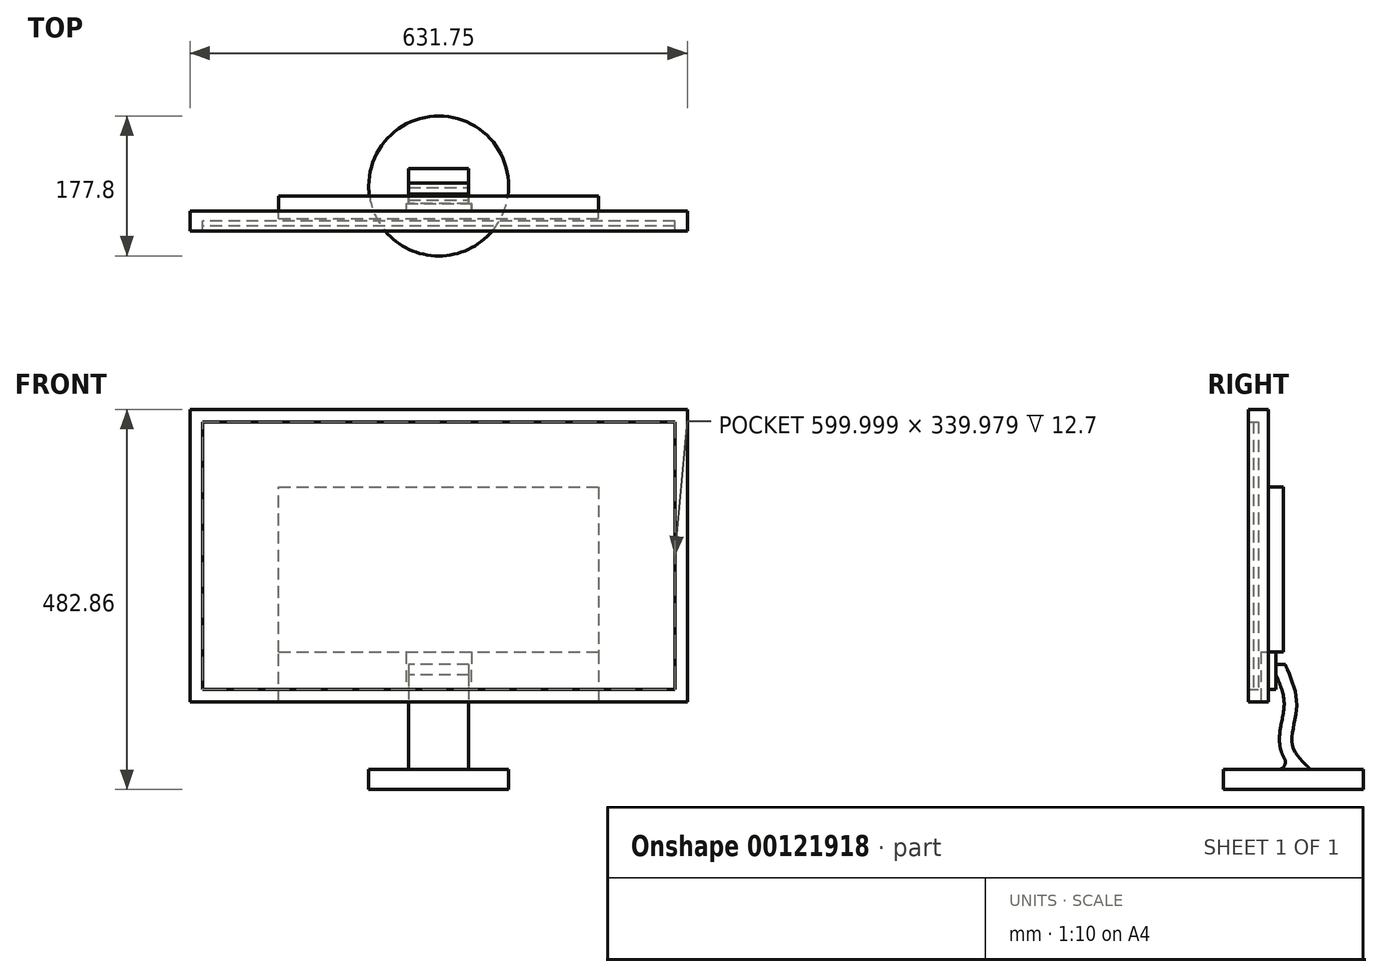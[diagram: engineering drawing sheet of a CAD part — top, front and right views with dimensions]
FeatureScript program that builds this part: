
annotation { "Feature Type Name" : "Feature", "Feature Type Description" : "" }
export const myFeature = defineFeature(function(context is Context, id is Id, definition is map)
    precondition{}
    {
        {
            var Q0;
            Q0=qCreatedBy(makeId("Front.planeOp"),FACE);
            var sketch = newSketch(context, id + "F0", { "sketchPlane" : qUnion([Q0])});
            skLineSegment(sketch, "E0.bottom", {"start": v(-325.58, 229.48) * mm, "end": v(306.17, 229.48) * mm});
            skLineSegment(sketch, "E0.top", {"start": v(-325.58, -142.25) * mm, "end": v(306.17, -142.25) * mm});
            skLineSegment(sketch, "E0.left", {"start": v(-325.58, 229.48) * mm, "end": v(-325.58, -142.25) * mm});
            skLineSegment(sketch, "E0.right", {"start": v(306.17, 229.48) * mm, "end": v(306.17, -142.25) * mm});
            skLineSegment(sketch, "E1", {"start": v(-309.7, 213.6) * mm, "end": v(-309.7, -126.38) * mm});
            skLineSegment(sketch, "E2", {"start": v(-309.7, -126.38) * mm, "end": v(290.3, -126.38) * mm});
            skLineSegment(sketch, "E3", {"start": v(290.3, -126.38) * mm, "end": v(290.3, 213.6) * mm});
            skLineSegment(sketch, "E4", {"start": v(290.3, 213.6) * mm, "end": v(-309.7, 213.6) * mm});
            skSolve(sketch);
        }
        {
            var Q0;
            Q0=makeQuery(id+"F0.imprint","IMPRINT",FACE,{"disambiguationData":[TD([[makeQuery(id+"F0.imprint","IMPRINT",EDGE,{"derivedFrom":sQuery(id+"F0.wireOp",EDGE,"E0.bottom")}),-1.0]])]});
            extrude(context, id + "F1", {"entities" : qUnion([Q0]), "depth" : 25.4 * mm});
        }
        {
            var Q0;
            Q0=makeQuery(id+"F0.imprint","IMPRINT",FACE,{"disambiguationData":[TD([[makeQuery(id+"F0.imprint","IMPRINT",EDGE,{"derivedFrom":sQuery(id+"F0.wireOp",EDGE,"E1")}),1.0]])]});
            extrude(context, id + "F2", {"entities" : qUnion([Q0]), "operationType" : NewBodyOperationType.ADD, "depth" : 12.7 * mm});
        }
        {
            var Q0;
            Q0=makeQuery(id+"F0.imprint","IMPRINT",FACE,{"disambiguationData":[TD([[makeQuery(id+"F0.imprint","IMPRINT",EDGE,{"derivedFrom":sQuery(id+"F0.wireOp",EDGE,"E1")}),1.0]])]});
            var sketch = newSketch(context, id + "F3", { "sketchPlane" : qUnion([Q0])});
            skLineSegment(sketch, "E5", {"start": v(-212.9, 130.8) * mm, "end": v(193.5, 130.8) * mm});
            skLineSegment(sketch, "E6", {"start": v(193.5, 130.8) * mm, "end": v(193.5, -78.75) * mm});
            skLineSegment(sketch, "E7", {"start": v(193.5, -78.75) * mm, "end": v(-212.9, -78.75) * mm});
            skLineSegment(sketch, "E8", {"start": v(-212.9, -78.75) * mm, "end": v(-212.9, 130.8) * mm});
            skSolve(sketch);
        }
        {
            var Q0;
            Q0=makeQuery(id+"F3.imprint","IMPRINT",FACE,{"disambiguationData":[TD([[makeQuery(id+"F3.imprint","IMPRINT",EDGE,{"derivedFrom":sQuery(id+"F3.wireOp",EDGE,"E5")}),-1.0]])]});
            extrude(context, id + "F4", {"entities" : qUnion([Q0]), "operationType" : NewBodyOperationType.ADD, "oppositeDirection" : true, "depth" : 19.05 * mm});
        }
        {
            var Q0;
            Q0=makeQuery(id+"F0.imprint","IMPRINT",FACE,{"disambiguationData":[TD([[makeQuery(id+"F0.imprint","IMPRINT",EDGE,{"derivedFrom":sQuery(id+"F0.wireOp",EDGE,"E1")}),1.0]])]});
            var sketch = newSketch(context, id + "F5", { "sketchPlane" : qUnion([Q0])});
            skPoint(sketch, "E9.0", {"position": v(193.5, -78.75) * mm});
            skPoint(sketch, "E10.0", {"position": v(-212.9, -78.75) * mm});
            skLineSegment(sketch, "E11", {"start": v(193.5, -78.75) * mm, "end": v(193.5, -142.25) * mm});
            skLineSegment(sketch, "E12", {"start": v(193.5, -142.25) * mm, "end": v(-212.9, -142.25) * mm});
            skLineSegment(sketch, "E13", {"start": v(-212.9, -142.25) * mm, "end": v(-212.9, -78.75) * mm});
            skLineSegment(sketch, "E14", {"start": v(-212.9, -78.75) * mm, "end": v(193.5, -78.75) * mm});
            skSolve(sketch);
        }
        {
            var Q0;
            {var subQ5=sQuery(id+"F5.wireOp",EDGE,"E12");Q0=makeQuery(id+"F5.imprint","IMPRINT",FACE,{"disambiguationData":[TD([[makeQuery(id+"F5.imprint","IMPRINT",EDGE,{"derivedFrom":subQ5}),-1.0]])]});}
            var Q1;
            {var subQ5=sQuery(id+"F5.wireOp",EDGE,"E14");Q1=makeQuery(id+"F5.imprint","IMPRINT",FACE,{"disambiguationData":[TD([[makeQuery(id+"F5.imprint","IMPRINT",EDGE,{"derivedFrom":subQ5}),-1.0]])]});}
            extrude(context, id + "F6", {"entities" : qUnion([Q0, Q1]), "operationType" : NewBodyOperationType.REMOVE, "depth" : 9.52 * mm});
        }
        {
            var Q0;
            {var subQ5=sQuery(id+"F5.wireOp",EDGE,"E14");Q0=makeQuery(id+"F5.imprint","IMPRINT",FACE,{"disambiguationData":[TD([[makeQuery(id+"F5.imprint","IMPRINT",EDGE,{"derivedFrom":subQ5}),-1.0]])]});}
            var sketch = newSketch(context, id + "F7", { "sketchPlane" : qUnion([Q0])});
            skLineSegment(sketch, "E15", {"start": v(31.57, -126.38) * mm, "end": v(-50.98, -126.38) * mm});
            skPoint(sketch, "E16.0", {"position": v(-212.9, -78.75) * mm});
            skLineSegment(sketch, "E17", {"start": v(-50.98, -78.75) * mm, "end": v(31.57, -78.75) * mm});
            skLineSegment(sketch, "E18", {"start": v(-50.98, -78.75) * mm, "end": v(-50.98, -126.38) * mm});
            skLineSegment(sketch, "E19", {"start": v(32, -78.67) * mm, "end": v(31.57, -126.38) * mm});
            skSolve(sketch);
        }
        {
            var Q0;
            {var subQ5=sQuery(id+"F7.wireOp",EDGE,"E15");Q0=makeQuery(id+"F7.imprint","IMPRINT",FACE,{"disambiguationData":[TD([[makeQuery(id+"F7.imprint","IMPRINT",EDGE,{"derivedFrom":subQ5}),1.0]])]});}
            extrude(context, id + "F8", {"entities" : qUnion([Q0]), "operationType" : NewBodyOperationType.ADD, "oppositeDirection" : true, "depth" : 9.52 * mm});
        }
        {
            var Q0;
            Q0=makeQuery(id+"F8.opExtrude","CAP_FACE",FACE,{"disambiguationData":[OSD([sQuery(id+"F5.wireOp",EDGE,"E14"),sQuery(id+"F7.wireOp",EDGE,"E15"),sQuery(id+"F7.wireOp",EDGE,"E17"),sQuery(id+"F7.wireOp",EDGE,"E18"),sQuery(id+"F7.wireOp",EDGE,"E19")])],"isStart":false});
            var sketch = newSketch(context, id + "F9", { "sketchPlane" : qUnion([Q0])});
            skLineSegment(sketch, "E20", {"start": v(-28.68, -94.63) * mm, "end": v(47.8, -94.63) * mm});
            skLineSegment(sketch, "E21", {"start": v(47.8, -94.63) * mm, "end": v(47.8, -126.38) * mm});
            skLineSegment(sketch, "E22", {"start": v(47.8, -126.38) * mm, "end": v(-28.68, -126.38) * mm});
            skLineSegment(sketch, "E23", {"start": v(-28.68, -94.63) * mm, "end": v(-28.68, -126.38) * mm});
            skSolve(sketch);
        }
        {
            var Q0;
            Q0=makeQuery(id+"F9.imprint","IMPRINT",FACE,{"disambiguationData":[TD([[makeQuery(id+"F9.imprint","IMPRINT",EDGE,{"derivedFrom":sQuery(id+"F9.wireOp",EDGE,"E20")}),-1.0]])]});
            extrude(context, id + "F10", {"entities" : qUnion([Q0]), "operationType" : NewBodyOperationType.ADD, "depth" : 44.45 * mm});
        }
        {
            var Q0;
            Q0=makeQuery(id+"F10.boolean.opBoolean","MERGE",FACE,{"derivedFrom":[makeQuery(id+"F8.opExtrude","SWEPT_FACE",FACE,{"disambiguationData":[OSD([sQuery(id+"F7.wireOp",EDGE,"E15")])]}),makeQuery(id+"F10.opExtrude","SWEPT_FACE",FACE,{"disambiguationData":[OSD([sQuery(id+"F9.wireOp",EDGE,"E22")])]})]});
            var sketch = newSketch(context, id + "F11", { "sketchPlane" : qUnion([Q0])});
            skLineSegment(sketch, "E24", {"start": v(28.68, -9.53) * mm, "end": v(-47.8, -9.53) * mm});
            skLineSegment(sketch, "E25", {"start": v(-47.8, -9.52) * mm, "end": v(-47.8, -53.98) * mm});
            skLineSegment(sketch, "E26", {"start": v(-47.8, -53.98) * mm, "end": v(28.68, -53.98) * mm});
            skLineSegment(sketch, "E27", {"start": v(28.68, -53.98) * mm, "end": v(28.68, -9.52) * mm});
            skSolve(sketch);
        }
        {
            var Q0;
            Q0=makeQuery(id+"F11.imprint","IMPRINT",FACE,{"disambiguationData":[TD([[makeQuery(id+"F11.imprint","IMPRINT",EDGE,{"derivedFrom":sQuery(id+"F11.wireOp",EDGE,"E24")}),1.0]])]});
            extrude(context, id + "F12", {"entities" : qUnion([Q0]), "operationType" : NewBodyOperationType.ADD, "depth" : 101.6 * mm});
        }
        {
            var Q0;
            Q0=makeQuery(id+"F12.opExtrude","CAP_FACE",FACE,{"disambiguationData":[OSD([sQuery(id+"F11.wireOp",EDGE,"E24"),sQuery(id+"F11.wireOp",EDGE,"E25"),sQuery(id+"F11.wireOp",EDGE,"E26"),sQuery(id+"F11.wireOp",EDGE,"E27")])],"isStart":false});
            var sketch = newSketch(context, id + "F13", { "sketchPlane" : qUnion([Q0])});
            skCircle(sketch, "E28", {"center": v(-9.56, -31.75) * mm, "radius": 88.9 * mm});
            skPoint(sketch, "E28.centerSnap0", {"position": v(-9.56, -53.98) * mm});
            skPoint(sketch, "E28.centerSnap1", {"position": v(28.68, -31.75) * mm});
            skSolve(sketch);
        }
        {
            var Q0;
            Q0=qSketchRegion(id+"F13",true);
            extrude(context, id + "F14", {"entities" : qUnion([Q0]), "operationType" : NewBodyOperationType.ADD, "depth" : 25.4 * mm});
        }
        {
            var Q0;
            Q0=makeQuery(id+"F12.boolean.opBoolean","MERGE",FACE,{"derivedFrom":[makeQuery(id+"F10.opExtrude","SWEPT_FACE",FACE,{"disambiguationData":[OSD([sQuery(id+"F9.wireOp",EDGE,"E21")])]}),makeQuery(id+"F12.opExtrude","SWEPT_FACE",FACE,{"disambiguationData":[OSD([sQuery(id+"F11.wireOp",EDGE,"E25")])]})]});
            var sketch = newSketch(context, id + "F15", { "sketchPlane" : qUnion([Q0])});
            skFitSpline(sketch, "E29", {"points": [v(-21.2, -94.63) * mm, v(-35.71, -146.34) * mm, v(-30.35, -196.38) * mm, v(-53.98, -227.98) * mm], "startDerivative": vector(-63.14, -143.08) * mm, "endDerivative": vector(-104.86, -93.64) * mm});
            skFitSpline(sketch, "E30.0", {"points": [v(-6.68, -101.04) * mm, v(-8, -104.02) * mm, v(-10.57, -109.85) * mm, v(-14.01, -118.26) * mm, v(-16.36, -124.97) * mm, v(-17.83, -130.15) * mm, v(-18.7, -133.95) * mm, v(-19.35, -137.66) * mm, v(-19.68, -140.68) * mm, v(-19.82, -143.06) * mm, v(-19.86, -144.54) * mm, v(-19.85, -145.72) * mm, v(-19.82, -146.9) * mm, v(-19.74, -148.44) * mm, v(-19.58, -150.36) * mm, v(-19.27, -153.02) * mm, v(-18.75, -156.52) * mm, v(-17.95, -160.96) * mm, v(-17.04, -165.6) * mm, v(-16.1, -170.43) * mm, v(-15.19, -175.44) * mm, v(-14.43, -180.62) * mm, v(-13.93, -186.02) * mm, v(-13.84, -190.72) * mm, v(-14.07, -194.6) * mm, v(-14.36, -197.09) * mm, v(-14.66, -198.85) * mm, v(-14.85, -199.86) * mm, v(-15.17, -201.36) * mm, v(-15.74, -203.57) * mm, v(-16.67, -206.4) * mm, v(-17.75, -209.12) * mm, v(-18.97, -211.7) * mm, v(-20.74, -215) * mm, v(-23.2, -218.84) * mm, v(-26.4, -223.02) * mm, v(-29.75, -226.85) * mm, v(-33.18, -230.4) * mm, v(-37.8, -234.82) * mm, v(-41.22, -237.87) * mm, v(-43.4, -239.82) * mm]});
            skLineSegment(sketch, "E31.0", {"start": v(-15.88, -126.38) * mm, "end": v(-15.88, -100.98) * mm});
            skLineSegment(sketch, "E31.1", {"start": v(-15.88, -221.63) * mm, "end": v(-15.88, -126.38) * mm});
            skLineSegment(sketch, "E31.2", {"start": v(-47.62, -221.63) * mm, "end": v(-15.87, -221.63) * mm});
            skLineSegment(sketch, "E31.3", {"start": v(-47.62, -100.98) * mm, "end": v(-47.62, -221.63) * mm});
            skLineSegment(sketch, "E31.4", {"start": v(-15.88, -100.98) * mm, "end": v(-47.62, -100.98) * mm});
            skSolve(sketch);
        }
        {
            var Q0;
            {var subQ3=sQuery(id+"F15.wireOp",EDGE,"E31.3");Q0=makeQuery(id+"F15.imprint","IMPRINT",FACE,{"disambiguationData":[TD([[makeQuery(id+"F15.imprint","IMPRINT",EDGE,{"derivedFrom":subQ3}),1.0]])]});}
            var Q1;
            {var subQ8=sQuery(id+"F15.wireOp",EDGE,"E31.3");Q1=makeQuery(id+"F15.imprint","IMPRINT",FACE,{"disambiguationData":[TD([[makeQuery(id+"F15.imprint","IMPRINT",EDGE,{"derivedFrom":subQ8}),-1.0]])]});}
            var Q2;
            {var subQ1=sQuery(id+"F15.wireOp",EDGE,"E30.0");var subQ3=sQuery(id+"F15.wireOp",EDGE,"E31.0");var subQ5=makeQuery(id+"F15.imprint","INTERSECT",VERTEX,{"derivedFrom":[subQ1,subQ3]});Q2=makeQuery(id+"F15.imprint","IMPRINT",FACE,{"disambiguationData":[TD([[makeQuery(id+"F15.imprint","IMPRINT",EDGE,{"disambiguationData":[TD([[subQ5,-1.0]])],"derivedFrom":subQ1}),1.0]])]});}
            var Q3;
            {var subQ0=sQuery(id+"F11.wireOp",EDGE,"E25");var subQ4=makeQuery(id+"F12.opExtrude","SWEPT_EDGE",EDGE,{"disambiguationData":[OSD([sQuery(id+"F7.wireOp",EDGE,"E15"),sQuery(id+"F11.wireOp",EDGE,"E24"),subQ0])]});Q3=makeQuery(id+"F15.imprint","IMPRINT",FACE,{"disambiguationData":[TD([[makeQuery(id+"F15.imprint","IMPRINT",EDGE,{"derivedFrom":subQ4}),1.0]])]});}
            var Q4;
            {var subQ1=sQuery(id+"F15.wireOp",EDGE,"E30.0");var subQ3=sQuery(id+"F15.wireOp",EDGE,"E31.1");var subQ5=makeQuery(id+"F15.imprint","INTERSECT",VERTEX,{"disambiguationData":[OD(1.0)],"derivedFrom":[subQ1,subQ3]});Q4=makeQuery(id+"F15.imprint","IMPRINT",FACE,{"disambiguationData":[TD([[makeQuery(id+"F15.imprint","IMPRINT",EDGE,{"disambiguationData":[TD([[subQ5,-1.0]])],"derivedFrom":subQ1}),1.0]])]});}
            extrude(context, id + "F16", {"entities" : qUnion([Q0, Q1, Q2, Q3, Q4]), "operationType" : NewBodyOperationType.REMOVE, "endBound" : BoundingType.UP_TO_NEXT, "oppositeDirection" : true, "depth" : 25.4 * mm});
        }
        {
            var Q0;
            Q0=makeQuery(id+"F16.boolean.opBoolean","COPY",EDGE,{"derivedFrom":makeQuery(id+"F16.opExtrude","SWEPT_EDGE",EDGE,{"disambiguationData":[OSD([sQuery(id+"F9.wireOp",EDGE,"E20"),sQuery(id+"F9.wireOp",EDGE,"E21"),sQuery(id+"F15.wireOp",EDGE,"E29")])]})});
            var Q1;
            {var subQ0=sQuery(id+"F11.wireOp",EDGE,"E26");Q1=makeQuery(id+"F16.boolean.opBoolean","MERGE",EDGE,{"derivedFrom":[makeQuery(id+"F12.opExtrude","CAP_EDGE",EDGE,{"disambiguationData":[OSD([subQ0])],"isStart":false}),makeQuery(id+"F16.opExtrude","SWEPT_EDGE",EDGE,{"disambiguationData":[OSD([subQ0,sQuery(id+"F11.wireOp",EDGE,"E27")])]})]});}
            var Q2;
            Q2=makeQuery(id+"F16.boolean.opBoolean","COPY",EDGE,{"derivedFrom":makeQuery(id+"F16.opExtrude","SWEPT_EDGE",EDGE,{"disambiguationData":[OSD([sQuery(id+"F11.wireOp",EDGE,"E25"),sQuery(id+"F15.wireOp",EDGE,"E30.0")])]})});
            var Q3;
            Q3=makeQuery(id+"F12.opExtrude","CAP_EDGE",EDGE,{"disambiguationData":[OSD([sQuery(id+"F11.wireOp",EDGE,"E25")])],"isStart":false});
            var Q4;
            Q4=makeQuery(id+"F12.opExtrude","CAP_EDGE",EDGE,{"disambiguationData":[OSD([sQuery(id+"F11.wireOp",EDGE,"E27")])],"isStart":false});
            fillet(context, id + "F17", {"entities" : qUnion([Q0, Q1, Q2, Q3, Q4]), "radius" : 9.34 * mm, "tangentPropagation" : true, "allowEdgeOverflow" : false});
        }
        {
            var Q0;
            Q0=makeQuery(id+"F2.opExtrude","CAP_FACE",FACE,{"disambiguationData":[OSD([sQuery(id+"F0.wireOp",EDGE,"E1"),sQuery(id+"F0.wireOp",EDGE,"E2"),sQuery(id+"F0.wireOp",EDGE,"E3"),sQuery(id+"F0.wireOp",EDGE,"E4")])],"isStart":false});
            extrude(context, id + "F18", {"entities" : qUnion([Q0]), "depth" : 6.35 * mm});
        }
    });
